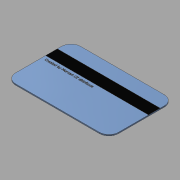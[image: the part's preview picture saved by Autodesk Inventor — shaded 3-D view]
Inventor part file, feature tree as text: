
AUTODESK INVENTOR PART (.ipt)
format: ipt  version: 2014 SP2 (Build 180246200, 246)  size: 1,224,192 bytes
history: native  units: mm
features: other x11, sketch x4, extrude x1, fillet x1, projected_geometry x1
ambient origin geometry x8: Origin, YZ Plane, XZ Plane, XY Plane, X Axis, Y Axis, Z Axis, Center Point
bodies: Body1 (feature_tree), Body2 (feature_tree), Body3 (feature_tree)
feature tree (18):
  other  "Těleso1"
  extrude  "Vysunutí1"  Depth=85.5mm
  fillet  "Zaoblení1"  Radius=54.0mm
  sketch  "Náčrt5"
  other  "Pracovní rovina1"
  other  "Pracovní rovina2"
  other  "Rozdělit1"
  other  "Rozdělit2"
  other  "Reliéf1"
  other  "Reliéf2"
  sketch  "Náčrt4"
  projected_geometry  "Promítnutá smyčka1"
  sketch  "Náčrt6"
  sketch  "Náčrt7"
  other  "Těleso2"
  other  "Těleso3"
  other  "Těleso4"
  other  "Těleso5"
